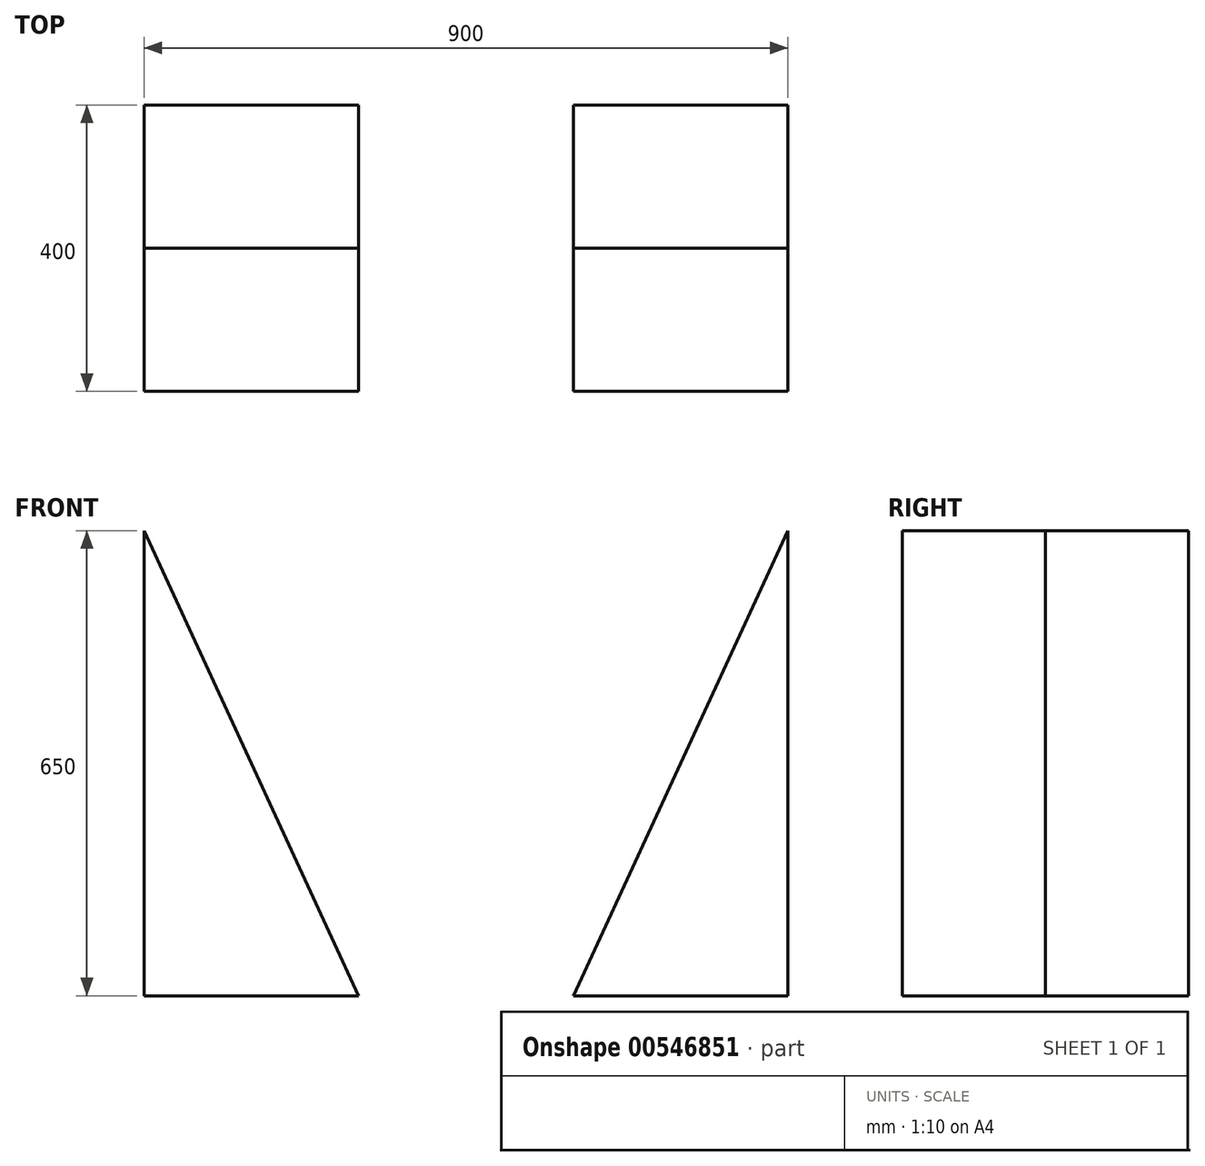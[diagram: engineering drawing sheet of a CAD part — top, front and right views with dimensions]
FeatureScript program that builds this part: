
annotation { "Feature Type Name" : "Feature", "Feature Type Description" : "" }
export const myFeature = defineFeature(function(context is Context, id is Id, definition is map)
    precondition{}
    {
        {
            var Q0;
            Q0=qCreatedBy(makeId("Front.planeOp"),FACE);
            var sketch = newSketch(context, id + "F0", { "sketchPlane" : qUnion([Q0])});
            skLineSegment(sketch, "E0.bottom", {"start": v(450, 325) * mm, "end": v(150, 325) * mm});
            skLineSegment(sketch, "E0.top", {"start": v(450, -325) * mm, "end": v(-450, -325) * mm});
            skLineSegment(sketch, "E0.left", {"start": v(450, 325) * mm, "end": v(450, -325) * mm});
            skLineSegment(sketch, "E0.right", {"start": v(-450, 325) * mm, "end": v(-450, -325) * mm});
            skPoint(sketch, "E0.middle", {"position": v(0, 0) * mm});
            skLineSegment(sketch, "E1", {"start": v(-150, -325) * mm, "end": v(-450, -325) * mm});
            skLineSegment(sketch, "E2", {"start": v(150, -325) * mm, "end": v(450, -325) * mm});
            skLineSegment(sketch, "E3", {"start": v(-450, 325) * mm, "end": v(-150, -325) * mm});
            skLineSegment(sketch, "E4", {"start": v(450, 325) * mm, "end": v(150, -325) * mm});
            skLineSegment(sketch, "E5", {"start": v(450, -325) * mm, "end": v(450, 325) * mm});
            skLineSegment(sketch, "E6", {"start": v(-450, 325) * mm, "end": v(-150, 325) * mm});
            skLineSegment(sketch, "E7", {"start": v(-150, 325) * mm, "end": v(-150, 75) * mm});
            skLineSegment(sketch, "E8", {"start": v(-150, 75) * mm, "end": v(150, 75) * mm});
            skLineSegment(sketch, "E9", {"start": v(150, 75) * mm, "end": v(150, 325) * mm});
            skLineSegment(sketch, "E10", {"start": v(150, 325) * mm, "end": v(450, 325) * mm});
            skLineSegment(sketch, "E11", {"start": v(-150, 325) * mm, "end": v(-450, 325) * mm});
            skSolve(sketch);
        }
        {
            var Q0;
            Q0=makeQuery(id+"F0.imprint","IMPRINT",FACE,{"disambiguationData":[TD([[makeQuery(id+"F0.imprint","IMPRINT",EDGE,{"derivedFrom":sQuery(id+"F0.wireOp",EDGE,"E3")}),-1.0]])]});
            var Q1;
            Q1=makeQuery(id+"F0.imprint","IMPRINT",FACE,{"disambiguationData":[TD([[makeQuery(id+"F0.imprint","IMPRINT",EDGE,{"derivedFrom":sQuery(id+"F0.wireOp",EDGE,"E4")}),1.0]])]});
            extrude(context, id + "F1", {"entities" : qUnion([Q0, Q1]), "depth" : 400 * mm, "offsetDistance" : 25 * mm});
        }
        {
            var Q0;
            Q0=makeQuery(id+"F0.imprint","IMPRINT",FACE,{"disambiguationData":[TD([[makeQuery(id+"F0.imprint","IMPRINT",EDGE,{"derivedFrom":sQuery(id+"F0.wireOp",EDGE,"E0.top")}),-1.0]])]});
            extrude(context, id + "F2", {"entities" : qUnion([Q0]), "depth" : 200 * mm, "offsetDistance" : 25 * mm});
        }
    });
